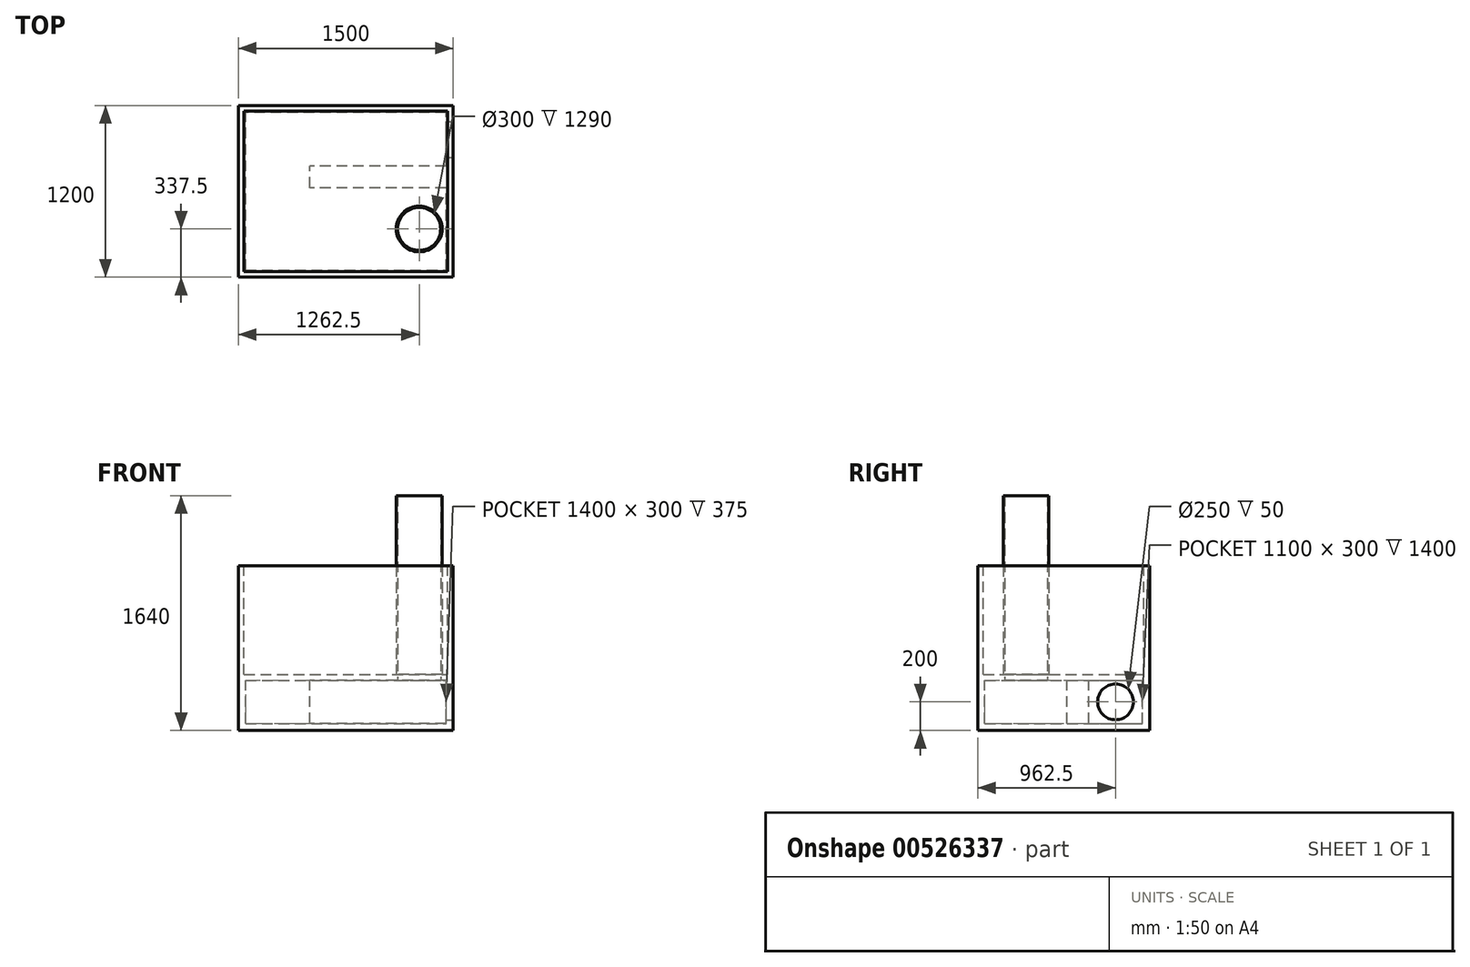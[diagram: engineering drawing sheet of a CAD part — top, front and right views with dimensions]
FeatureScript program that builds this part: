
annotation { "Feature Type Name" : "Feature", "Feature Type Description" : "" }
export const myFeature = defineFeature(function(context is Context, id is Id, definition is map)
    precondition{}
    {
        {
            var Q0;
            Q0=qCreatedBy(makeId("Front.planeOp"),FACE);
            var sketch = newSketch(context, id + "F0", { "sketchPlane" : qUnion([Q0])});
            skLineSegment(sketch, "E0.bottom", {"start": v(0, 0) * mm, "end": v(1500, 0) * mm});
            skLineSegment(sketch, "E0.top", {"start": v(0, 800) * mm, "end": v(1500, 800) * mm});
            skLineSegment(sketch, "E0.left", {"start": v(0, 0) * mm, "end": v(0, 800) * mm});
            skLineSegment(sketch, "E0.right", {"start": v(1500, 0) * mm, "end": v(1500, 800) * mm});
            skSolve(sketch);
        }
        {
            var Q0;
            Q0=makeQuery(id+"F0.imprint","IMPRINT",FACE,{"disambiguationData":[TD([[makeQuery(id+"F0.imprint","IMPRINT",EDGE,{"derivedFrom":sQuery(id+"F0.wireOp",EDGE,"E0.bottom")}),1.0]])]});
            extrude(context, id + "F1", {"entities" : qUnion([Q0]), "depth" : 1200 * mm, "offsetDistance" : 25 * mm});
        }
        {
            var Q0;
            Q0=makeQuery(id+"F1.opExtrude","SWEPT_FACE",FACE,{"disambiguationData":[OSD([sQuery(id+"F0.wireOp",EDGE,"E0.top")])]});
            shell(context, id + "F2", {"entities" : qUnion([Q0]), "thickness" : 40 * mm});
        }
        {
            var Q0;
            Q0=makeQuery(id+"F1.opExtrude","SWEPT_FACE",FACE,{"disambiguationData":[OSD([sQuery(id+"F0.wireOp",EDGE,"E0.bottom")])]});
            var sketch = newSketch(context, id + "F3", { "sketchPlane" : qUnion([Q0])});
            skLineSegment(sketch, "E1.top", {"start": v(1500, 50) * mm, "end": v(50, 50) * mm});
            skLineSegment(sketch, "E1.right", {"start": v(50, 1150) * mm, "end": v(50, 50) * mm});
            skLineSegment(sketch, "E2.bottom", {"start": v(1500, 0) * mm, "end": v(0, 0) * mm});
            skLineSegment(sketch, "E2.top", {"start": v(1500, 1200) * mm, "end": v(0, 1200) * mm});
            skLineSegment(sketch, "E2.left", {"start": v(1500, 0) * mm, "end": v(1500, 50) * mm});
            skLineSegment(sketch, "E2.right", {"start": v(0, 0) * mm, "end": v(0, 1200) * mm});
            skPoint(sketch, "E3.orphan", {"position": v(0, 600) * mm});
            skLineSegment(sketch, "E4.trimOffspring", {"start": v(1500, 1150) * mm, "end": v(1500, 1200) * mm});
            skLineSegment(sketch, "E5", {"start": v(50, 1150) * mm, "end": v(1500, 1150) * mm});
            skSolve(sketch);
        }
        {
            var Q0;
            Q0=makeQuery(id+"F3.imprint","IMPRINT",FACE,{"disambiguationData":[TD([[makeQuery(id+"F3.imprint","IMPRINT",EDGE,{"derivedFrom":sQuery(id+"F3.wireOp",EDGE,"E1.top")}),1.0]])]});
            extrude(context, id + "F4", {"entities" : qUnion([Q0]), "operationType" : NewBodyOperationType.ADD, "depth" : 300 * mm, "offsetDistance" : 25 * mm});
        }
        {
            var Q0;
            Q0=makeQuery(id+"F1.opExtrude","SWEPT_FACE",FACE,{"disambiguationData":[OSD([sQuery(id+"F0.wireOp",EDGE,"E0.bottom")])]});
            var sketch = newSketch(context, id + "F5", { "sketchPlane" : qUnion([Q0])});
            skPoint(sketch, "E6.orphan", {"position": v(50, 600) * mm});
            skLineSegment(sketch, "E7.bottom", {"start": v(1500, 575) * mm, "end": v(500, 575) * mm});
            skLineSegment(sketch, "E7.top", {"start": v(1500, 425) * mm, "end": v(500, 425) * mm});
            skLineSegment(sketch, "E7.left", {"start": v(1500, 575) * mm, "end": v(1500, 425) * mm});
            skLineSegment(sketch, "E7.right", {"start": v(500, 575) * mm, "end": v(500, 425) * mm});
            skSolve(sketch);
        }
        {
            var Q0;
            Q0=makeQuery(id+"F5.imprint","IMPRINT",FACE,{"disambiguationData":[TD([[makeQuery(id+"F5.imprint","IMPRINT",EDGE,{"derivedFrom":sQuery(id+"F5.wireOp",EDGE,"E7.bottom")}),1.0]])]});
            extrude(context, id + "F6", {"entities" : qUnion([Q0]), "operationType" : NewBodyOperationType.ADD, "depth" : 300 * mm, "offsetDistance" : 25 * mm});
        }
        {
            var Q0;
            Q0=makeQuery(id+"F1.opExtrude","SWEPT_FACE",FACE,{"disambiguationData":[OSD([sQuery(id+"F0.wireOp",EDGE,"E0.bottom")])]});
            var sketch = newSketch(context, id + "F7", { "sketchPlane" : qUnion([Q0])});
            skLineSegment(sketch, "E8.bottom", {"start": v(1500, 1150) * mm, "end": v(1450, 1150) * mm});
            skLineSegment(sketch, "E8.top", {"start": v(1500, 575) * mm, "end": v(1450, 575) * mm});
            skLineSegment(sketch, "E8.left", {"start": v(1500, 1150) * mm, "end": v(1500, 575) * mm});
            skLineSegment(sketch, "E8.right", {"start": v(1450, 1150) * mm, "end": v(1450, 575) * mm});
            skSolve(sketch);
        }
        {
            var Q0;
            Q0=makeQuery(id+"F7.imprint","IMPRINT",FACE,{"disambiguationData":[TD([[makeQuery(id+"F7.imprint","IMPRINT",EDGE,{"derivedFrom":sQuery(id+"F7.wireOp",EDGE,"E8.bottom")}),-1.0]])]});
            extrude(context, id + "F8", {"entities" : qUnion([Q0]), "operationType" : NewBodyOperationType.ADD, "depth" : 300 * mm, "offsetDistance" : 25 * mm});
        }
        {
            var Q0;
            Q0=makeQuery(id+"F8.boolean.opBoolean","MERGE",FACE,{"derivedFrom":[makeQuery(id+"F6.boolean.opBoolean","MERGE",FACE,{"derivedFrom":[makeQuery(id+"F4.boolean.opBoolean","MERGE",FACE,{"derivedFrom":[makeQuery(id+"F1.opExtrude","SWEPT_FACE",FACE,{"disambiguationData":[OSD([sQuery(id+"F0.wireOp",EDGE,"E0.right")])]}),makeQuery(id+"F4.opExtrude","SWEPT_FACE",FACE,{"disambiguationData":[OSD([sQuery(id+"F3.wireOp",EDGE,"E2.left")])]}),makeQuery(id+"F4.opExtrude","SWEPT_FACE",FACE,{"disambiguationData":[OSD([sQuery(id+"F3.wireOp",EDGE,"E4.trimOffspring")])]})]}),makeQuery(id+"F6.opExtrude","SWEPT_FACE",FACE,{"disambiguationData":[OSD([sQuery(id+"F5.wireOp",EDGE,"E7.left")])]})]}),makeQuery(id+"F8.opExtrude","SWEPT_FACE",FACE,{"disambiguationData":[OSD([sQuery(id+"F7.wireOp",EDGE,"E8.left")])]})]});
            var sketch = newSketch(context, id + "F9", { "sketchPlane" : qUnion([Q0])});
            skLineSegment(sketch, "E9.bottom", {"start": v(-425, 0) * mm, "end": v(-50, 0) * mm});
            skLineSegment(sketch, "E9.top", {"start": v(-425, -300) * mm, "end": v(-50, -300) * mm});
            skLineSegment(sketch, "E9.left", {"start": v(-425, 0) * mm, "end": v(-425, -300) * mm});
            skLineSegment(sketch, "E9.right", {"start": v(-50, 0) * mm, "end": v(-50, -300) * mm});
            skCircle(sketch, "E10", {"center": v(-237.5, -150) * mm, "radius": 125 * mm});
            skPoint(sketch, "E11.start.orphan", {"position": v(-425, -150) * mm});
            skPoint(sketch, "E12.trimOffspring.end.orphan", {"position": v(-50, -150) * mm});
            skSolve(sketch);
        }
        {
            var Q0;
            Q0=makeQuery(id+"F9.imprint","IMPRINT",FACE,{"disambiguationData":[TD([[makeQuery(id+"F9.imprint","IMPRINT",EDGE,{"derivedFrom":sQuery(id+"F9.wireOp",EDGE,"E9.bottom")}),-1.0]])]});
            extrude(context, id + "F10", {"entities" : qUnion([Q0]), "operationType" : NewBodyOperationType.ADD, "oppositeDirection" : true, "depth" : 50 * mm, "offsetDistance" : 25 * mm});
        }
        {
            var Q0;
            Q0=makeQuery(id+"F1.opExtrude","SWEPT_FACE",FACE,{"disambiguationData":[OSD([sQuery(id+"F0.wireOp",EDGE,"E0.bottom")])]});
            var sketch = newSketch(context, id + "F11", { "sketchPlane" : qUnion([Q0])});
            skCircle(sketch, "E13", {"center": v(1262.5, 862.5) * mm, "radius": 150 * mm});
            skPoint(sketch, "E14.orphan", {"position": v(1075, 1150) * mm});
            skPoint(sketch, "E15.start.orphan", {"position": v(1450, 1150) * mm});
            skPoint(sketch, "E16.trimOffspring.end.orphan", {"position": v(1262.5, 575) * mm});
            skPoint(sketch, "E17.start.orphan", {"position": v(1262.5, 1150) * mm});
            skSolve(sketch);
        }
        {
            var Q0;
            Q0=makeQuery(id+"F11.imprint","IMPRINT",FACE,{"disambiguationData":[TD([[makeQuery(id+"F11.imprint","IMPRINT",EDGE,{"derivedFrom":sQuery(id+"F11.wireOp",EDGE,"E13")}),1.0]])]});
            extrude(context, id + "F12", {"entities" : qUnion([Q0]), "operationType" : NewBodyOperationType.REMOVE, "oppositeDirection" : true, "depth" : 50 * mm, "offsetDistance" : 25 * mm});
        }
        {
            var Q0;
            Q0=makeQuery(id+"F10.boolean.opBoolean","MERGE",FACE,{"derivedFrom":[makeQuery(id+"F8.boolean.opBoolean","MERGE",FACE,{"derivedFrom":[makeQuery(id+"F4.opExtrude","CAP_FACE",FACE,{"disambiguationData":[OSD([sQuery(id+"F3.wireOp",EDGE,"E1.top"),sQuery(id+"F3.wireOp",EDGE,"E1.right"),sQuery(id+"F3.wireOp",EDGE,"E2.bottom"),sQuery(id+"F3.wireOp",EDGE,"E2.top"),sQuery(id+"F3.wireOp",EDGE,"E2.left"),sQuery(id+"F3.wireOp",EDGE,"E2.right"),sQuery(id+"F3.wireOp",EDGE,"E4.trimOffspring"),sQuery(id+"F3.wireOp",EDGE,"E5")])],"isStart":false}),makeQuery(id+"F6.opExtrude","CAP_FACE",FACE,{"disambiguationData":[OSD([sQuery(id+"F5.wireOp",EDGE,"E7.bottom"),sQuery(id+"F5.wireOp",EDGE,"E7.top"),sQuery(id+"F5.wireOp",EDGE,"E7.left"),sQuery(id+"F5.wireOp",EDGE,"E7.right")])],"isStart":false}),makeQuery(id+"F8.opExtrude","CAP_FACE",FACE,{"disambiguationData":[OSD([sQuery(id+"F7.wireOp",EDGE,"E8.bottom"),sQuery(id+"F7.wireOp",EDGE,"E8.top"),sQuery(id+"F7.wireOp",EDGE,"E8.left"),sQuery(id+"F7.wireOp",EDGE,"E8.right")])],"isStart":false})]}),makeQuery(id+"F10.opExtrude","SWEPT_FACE",FACE,{"disambiguationData":[OSD([sQuery(id+"F9.wireOp",EDGE,"E9.top")])]})]});
            var sketch = newSketch(context, id + "F13", { "sketchPlane" : qUnion([Q0])});
            skLineSegment(sketch, "E18.bottom", {"start": v(0, 1200) * mm, "end": v(1500, 1200) * mm});
            skLineSegment(sketch, "E18.top", {"start": v(0, 0) * mm, "end": v(1500, 0) * mm});
            skLineSegment(sketch, "E18.left", {"start": v(0, 1200) * mm, "end": v(0, 0) * mm});
            skLineSegment(sketch, "E18.right", {"start": v(1500, 1200) * mm, "end": v(1500, 0) * mm});
            skSolve(sketch);
        }
        {
            var Q0;
            Q0 = qSketchRegion(id + "F13", true);
            extrude(context, id + "F14", {"entities" : qUnion([Q0]), "operationType" : NewBodyOperationType.ADD, "depth" : 50 * mm, "offsetDistance" : 25 * mm});
        }
        {
            var Q0;
            Q0=makeQuery(id+"F2.opShell","OFFSET_FACE",FACE,{"disambiguationData":[OSD([sQuery(id+"F0.wireOp",EDGE,"E0.bottom")])]});
            var sketch = newSketch(context, id + "F15", { "sketchPlane" : qUnion([Q0])});
            skCircle(sketch, "E19", {"center": v(1262.5, -862.5) * mm, "radius": 150 * mm});
            skPoint(sketch, "E19.first.point", {"position": v(1196.35, -727.87) * mm});
            skPoint(sketch, "E19.second.point", {"position": v(1362.06, -750.3) * mm});
            skPoint(sketch, "E19.third.point", {"position": v(1252.36, -1012.16) * mm});
            skCircle(sketch, "E20", {"center": v(1262.5, -862.5) * mm, "radius": 160 * mm});
            skSolve(sketch);
        }
        {
            var Q0;
            Q0 = qSketchRegion(id + "F15", true);
            extrude(context, id + "F16", {"entities" : qUnion([Q0]), "operationType" : NewBodyOperationType.ADD, "depth" : 1250 * mm, "offsetDistance" : 25 * mm});
        }
    });
